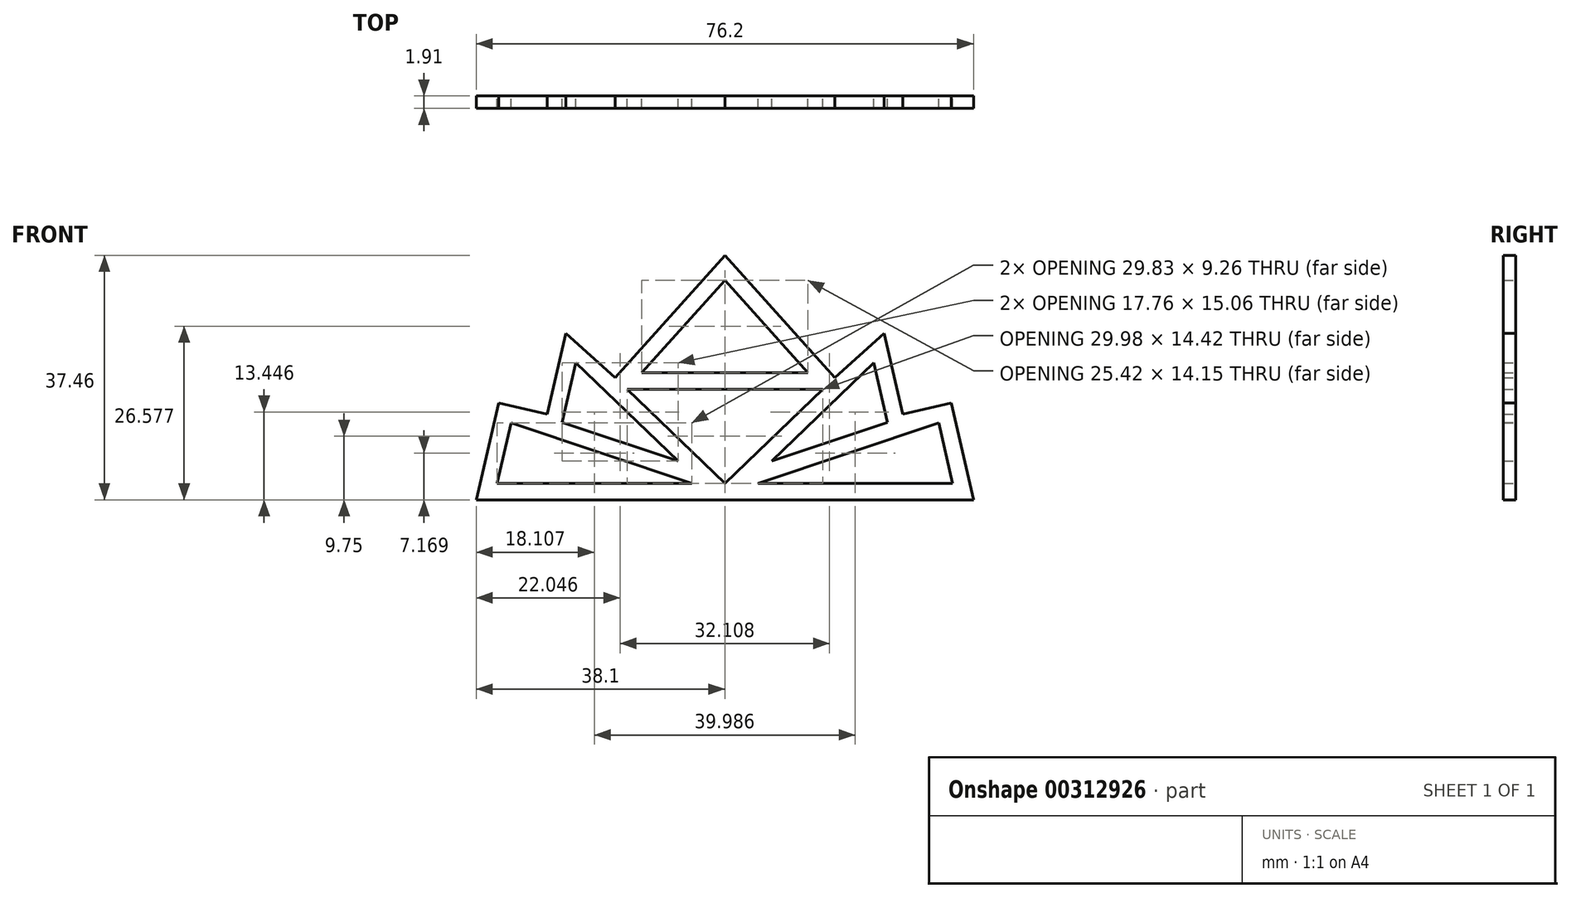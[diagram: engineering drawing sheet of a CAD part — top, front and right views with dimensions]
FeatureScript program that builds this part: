
annotation { "Feature Type Name" : "Feature", "Feature Type Description" : "" }
export const myFeature = defineFeature(function(context is Context, id is Id, definition is map)
    precondition{}
    {
        {
            var Q0;
            Q0=qCreatedBy(makeId("Front.planeOp"),FACE);
            var sketch = newSketch(context, id + "F0", { "sketchPlane" : qUnion([Q0])});
            skLineSegment(sketch, "E0", {"start": v(-45.4, -25.74) * mm, "end": v(30.8, -25.74) * mm});
            skLineSegment(sketch, "E1", {"start": v(30.8, -25.74) * mm, "end": v(27.37, -10.9) * mm});
            skLineSegment(sketch, "E2", {"start": v(27.37, -10.9) * mm, "end": v(19.94, -12.6) * mm});
            skLineSegment(sketch, "E3", {"start": v(19.94, -12.6) * mm, "end": v(17.09, -0.23) * mm});
            skLineSegment(sketch, "E4", {"start": v(17.09, -0.23) * mm, "end": v(9.53, -7.02) * mm});
            skLineSegment(sketch, "E5", {"start": v(9.53, -7.02) * mm, "end": v(-7.3, 11.72) * mm});
            skLineSegment(sketch, "E6", {"start": v(-7.3, 11.72) * mm, "end": v(-24.13, -7.02) * mm});
            skLineSegment(sketch, "E7", {"start": v(-24.13, -7.02) * mm, "end": v(-31.68, -0.23) * mm});
            skLineSegment(sketch, "E8", {"start": v(-31.68, -0.23) * mm, "end": v(-34.54, -12.6) * mm});
            skLineSegment(sketch, "E9", {"start": v(-34.54, -12.6) * mm, "end": v(-41.97, -10.9) * mm});
            skLineSegment(sketch, "E10", {"start": v(-41.97, -10.9) * mm, "end": v(-45.4, -25.74) * mm});
            skLineSegment(sketch, "E11", {"start": v(-7.3, 7.91) * mm, "end": v(-20, -6.24) * mm});
            skLineSegment(sketch, "E12", {"start": v(-20, -6.24) * mm, "end": v(5.4, -6.24) * mm});
            skLineSegment(sketch, "E13", {"start": v(5.4, -6.24) * mm, "end": v(-7.3, 7.91) * mm});
            skLineSegment(sketch, "E14", {"start": v(-22.3, -8.78) * mm, "end": v(7.7, -8.78) * mm});
            skLineSegment(sketch, "E15", {"start": v(7.7, -8.78) * mm, "end": v(-7.3, -23.2) * mm});
            skLineSegment(sketch, "E16", {"start": v(-7.3, -23.2) * mm, "end": v(-22.3, -8.78) * mm});
            skLineSegment(sketch, "E17", {"start": v(-40.07, -13.94) * mm, "end": v(-12.38, -23.2) * mm});
            skLineSegment(sketch, "E18", {"start": v(-12.38, -23.2) * mm, "end": v(-42.2, -23.2) * mm});
            skLineSegment(sketch, "E19", {"start": v(-42.2, -23.2) * mm, "end": v(-40.07, -13.94) * mm});
            skLineSegment(sketch, "E20", {"start": v(25.47, -13.94) * mm, "end": v(27.6, -23.2) * mm});
            skLineSegment(sketch, "E21", {"start": v(27.6, -23.2) * mm, "end": v(-2.22, -23.2) * mm});
            skLineSegment(sketch, "E22", {"start": v(-2.22, -23.2) * mm, "end": v(25.47, -13.94) * mm});
            skLineSegment(sketch, "E23", {"start": v(-30.13, -4.77) * mm, "end": v(-14.48, -19.82) * mm});
            skLineSegment(sketch, "E24", {"start": v(-14.48, -19.82) * mm, "end": v(-32.23, -13.88) * mm});
            skLineSegment(sketch, "E25", {"start": v(-32.23, -13.88) * mm, "end": v(-30.13, -4.77) * mm});
            skLineSegment(sketch, "E26", {"start": v(-0.12, -19.82) * mm, "end": v(15.53, -4.77) * mm});
            skLineSegment(sketch, "E27", {"start": v(15.53, -4.77) * mm, "end": v(17.63, -13.88) * mm});
            skLineSegment(sketch, "E28", {"start": v(17.63, -13.88) * mm, "end": v(-0.12, -19.82) * mm});
            skSolve(sketch);
        }
        {
            var Q0;
            Q0=makeQuery(id+"F0.imprint","IMPRINT",FACE,{"disambiguationData":[TD([[makeQuery(id+"F0.imprint","IMPRINT",EDGE,{"derivedFrom":sQuery(id+"F0.wireOp",EDGE,"E0")}),1.0]])]});
            extrude(context, id + "F1", {"entities" : qUnion([Q0]), "depth" : 1.9 * mm});
        }
    });
